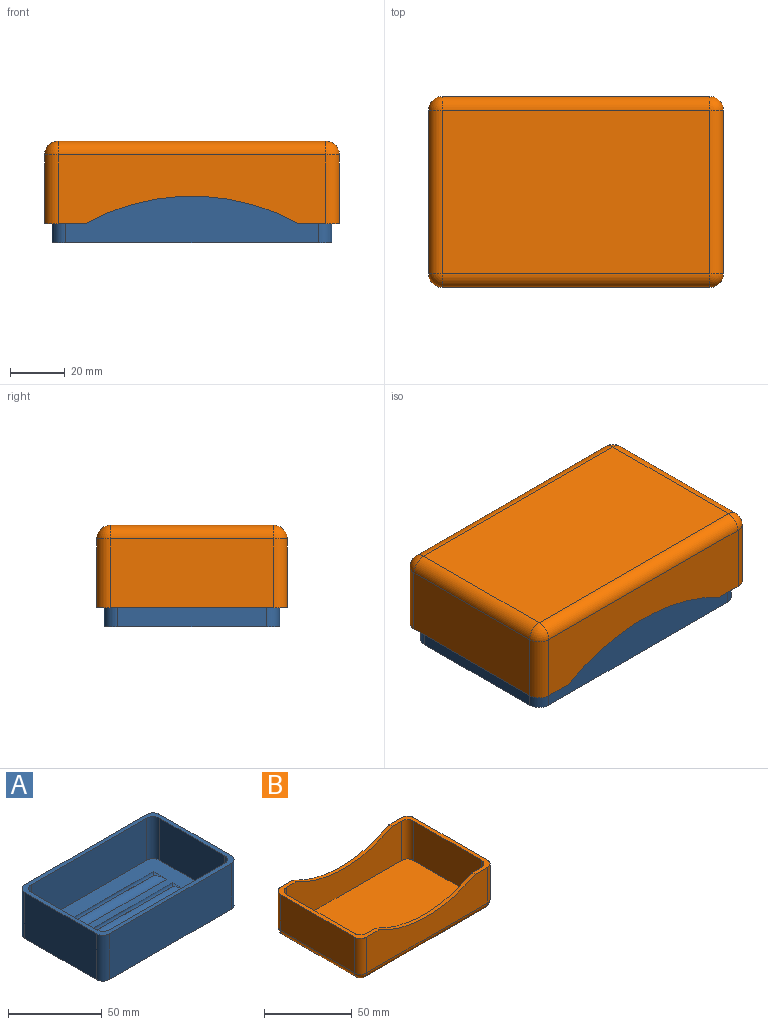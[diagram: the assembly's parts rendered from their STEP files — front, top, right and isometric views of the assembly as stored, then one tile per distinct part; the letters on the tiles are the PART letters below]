
ASSEMBLY  parts=2 mates=1
PART A: 34 faces, bbox 102x64x30 mm
  f0: plane 102x64mm, normal (0,0,1), area 805mm2, adj f1,f2,f3,f4,f6,f7,f8,f9
  f1: plane 92x30mm, normal (0,1,0), area 2760mm2, adj f0,f5,f30,f33
  f2: plane 54x30mm, normal (-1,0,0), area 1620mm2, adj f0,f5,f30,f31
  f3: plane 92x30mm, normal (0,-1,0), area 2760mm2, adj f0,f5,f31,f32
  f4: plane 54x30mm, normal (1,0,0), area 1620mm2, adj f0,f5,f32,f33
  f5: plane 102x64mm, normal (0,0,-1), area 6506.5mm2, adj f1,f2,f3,f4,f30,f31,f32,f33
  f6: plane 87x27.5mm, normal (0,-1,0), area 2392.5mm2, adj f0,f10,f27,f29
  f7: plane 49x27.5mm, normal (1,0,0), area 1347.5mm2, adj f0,f10,f28,f29
  f8: plane 87x27.5mm, normal (0,1,0), area 2392.5mm2, adj f0,f10,f26,f28
  f9: plane 49x27.5mm, normal (-1,0,0), area 1347.5mm2, adj f0,f10,f26,f27
  f10: plane 97x59mm, normal (0,0,1), area 3391.5mm2, adj f6,f7,f8,f9,f14,f15,f16,f17
  f11: plane 67.05x0.05mm, normal (0,0,1), area 3.4mm2, adj f22,f23,f24,f25
  f12: plane 67.05x0.05mm, normal (0,0,1), area 3.4mm2, adj f18,f19,f20,f21
  f13: plane 67.05x0.05mm, normal (0,0,1), area 3.4mm2, adj f14,f15,f16,f17
  f14: cylinder r=6.2mm len=10mm, axis (0,1,0), area 31.3mm2, adj f10,f13,f15,f16
  f15: cylinder r=6.2mm len=77mm, axis (1,0,0), area 418.2mm2, adj f10,f13,f14,f17
  f16: cylinder r=6.2mm len=77mm, axis (1,0,0), area 418.2mm2, adj f10,f13,f14,f17
  f17: cylinder r=6.2mm len=10mm, axis (0,1,0), area 31.3mm2, adj f10,f13,f15,f16
  f18: cylinder r=6.2mm len=10mm, axis (0,1,0), area 31.3mm2, adj f10,f12,f19,f20
  f19: cylinder r=6.2mm len=77mm, axis (1,0,0), area 418.2mm2, adj f10,f12,f18,f21
  f20: cylinder r=6.2mm len=77mm, axis (1,0,0), area 418.2mm2, adj f10,f12,f18,f21
  f21: cylinder r=6.2mm len=10mm, axis (0,1,0), area 31.3mm2, adj f10,f12,f19,f20
  f22: cylinder r=6.2mm len=10mm, axis (0,1,0), area 31.3mm2, adj f10,f11,f23,f24
  f23: cylinder r=6.2mm len=77mm, axis (1,0,0), area 418.2mm2, adj f10,f11,f22,f25
  f24: cylinder r=6.2mm len=77mm, axis (1,0,0), area 418.2mm2, adj f10,f11,f22,f25
  f25: cylinder r=6.2mm len=10mm, axis (0,1,0), area 31.3mm2, adj f10,f11,f23,f24
  f26: cylinder r=5mm len=27.5mm, axis (0,0,-1), area 216mm2, adj f0,f8,f9,f10
  f27: cylinder r=5mm len=27.5mm, axis (0,0,1), area 216mm2, adj f0,f6,f9,f10
  f28: cylinder r=5mm len=27.5mm, axis (0,0,1), area 216mm2, adj f0,f7,f8,f10
  f29: cylinder r=5mm len=27.5mm, axis (0,0,-1), area 216mm2, adj f0,f6,f7,f10
  f30: cylinder r=5mm len=30mm, axis (0,0,1), area 235.6mm2, adj f0,f1,f2,f5
  f31: cylinder r=5mm len=30mm, axis (0,0,-1), area 235.6mm2, adj f0,f2,f3,f5
  f32: cylinder r=5mm len=30mm, axis (0,0,1), area 235.6mm2, adj f0,f3,f4,f5
  f33: cylinder r=5mm len=30mm, axis (0,0,-1), area 235.6mm2, adj f0,f1,f4,f5
PART B: 30 faces, bbox 107.5x69.5x30 mm
  f0: plane 69.5x15mm, normal (0,0,1), area 236.2mm2, adj f1,f3,f5,f7,f9,f10,f12,f13
  f1: plane 97.5x25mm, normal (0,-1,0), area 1914mm2, adj f0,f2,f12,f17,f20,f22
  f2: plane 69.5x15mm, normal (0,0,1), area 236.3mm2, adj f1,f3,f4,f7,f8,f9,f12,f13
  f3: plane 97.5x25mm, normal (0,1,0), area 1914mm2, adj f0,f2,f13,f14,f18,f24
  f4: plane 59.5x25mm, normal (-1,0,0), area 1487.5mm2, adj f2,f15,f18,f20
  f5: plane 59.5x25mm, normal (1,0,0), area 1487.5mm2, adj f0,f16,f22,f24
  f6: plane 97.5x59.5mm, normal (0,0,-1), area 5801.2mm2, adj f14,f15,f16,f17
  f7: plane 92.5x27.5mm, normal (0,-1,0), area 2020.3mm2, adj f0,f2,f11,f13,f27,f29
  f8: plane 54.5x27.5mm, normal (1,0,0), area 1498.8mm2, adj f2,f11,f28,f29
  f9: plane 92.5x27.5mm, normal (0,1,0), area 2020.3mm2, adj f0,f2,f11,f12,f26,f28
  f10: plane 54.5x27.5mm, normal (-1,0,0), area 1498.8mm2, adj f0,f11,f26,f27
  f11: plane 102.5x64.5mm, normal (0,0,1), area 6589.8mm2, adj f7,f8,f9,f10,f26,f27,f28,f29
  f12: cylinder r=80.08mm len=77.5mm, axis (0,-1,0), area 202.2mm2, adj f0,f1,f2,f9
  f13: cylinder r=80.08mm len=77.5mm, axis (0,-1,0), area 202.2mm2, adj f0,f2,f3,f7
  f14: cylinder r=5mm len=97.5mm, axis (-1,0,0), area 765.8mm2, adj f3,f6,f19,f25
  f15: cylinder r=5mm len=59.5mm, axis (0,-1,0), area 467.3mm2, adj f4,f6,f19,f21
  f16: cylinder r=5mm len=59.5mm, axis (0,1,0), area 467.3mm2, adj f5,f6,f23,f25
  f17: cylinder r=5mm len=97.5mm, axis (1,0,0), area 765.8mm2, adj f1,f6,f21,f23
  f18: cylinder r=5mm len=25mm, axis (0,0,1), area 196.3mm2, adj f2,f3,f4,f19
  f19: sphere r=5mm, area 39.3mm2, adj f14,f15,f18
  f20: cylinder r=5mm len=25mm, axis (0,0,-1), area 196.3mm2, adj f1,f2,f4,f21
  f21: sphere r=5mm, area 39.3mm2, adj f15,f17,f20
  f22: cylinder r=5mm len=25mm, axis (0,0,1), area 196.3mm2, adj f0,f1,f5,f23
  f23: sphere r=5mm, area 39.3mm2, adj f16,f17,f22
  f24: cylinder r=5mm len=25mm, axis (0,0,-1), area 196.3mm2, adj f0,f3,f5,f25
  f25: sphere r=5mm, area 39.3mm2, adj f14,f16,f24
  f26: cylinder r=5mm len=27.5mm, axis (0,0,-1), area 216mm2, adj f0,f9,f10,f11
  f27: cylinder r=5mm len=27.5mm, axis (0,0,1), area 216mm2, adj f0,f7,f10,f11
  f28: cylinder r=5mm len=27.5mm, axis (0,0,1), area 216mm2, adj f2,f8,f9,f11
  f29: cylinder r=5mm len=27.5mm, axis (0,0,-1), area 216mm2, adj f2,f7,f8,f11
PLACE A t=(3.99,-40.45,0)mm fixed
PLACE B rot(axis=(0,1,0),180deg) t=(3.99,-40.45,37.02)mm
MATE slider B.f11 <-> A.f10  axis (0,0,-1) through (3.99,-40.45,34.52)mm
